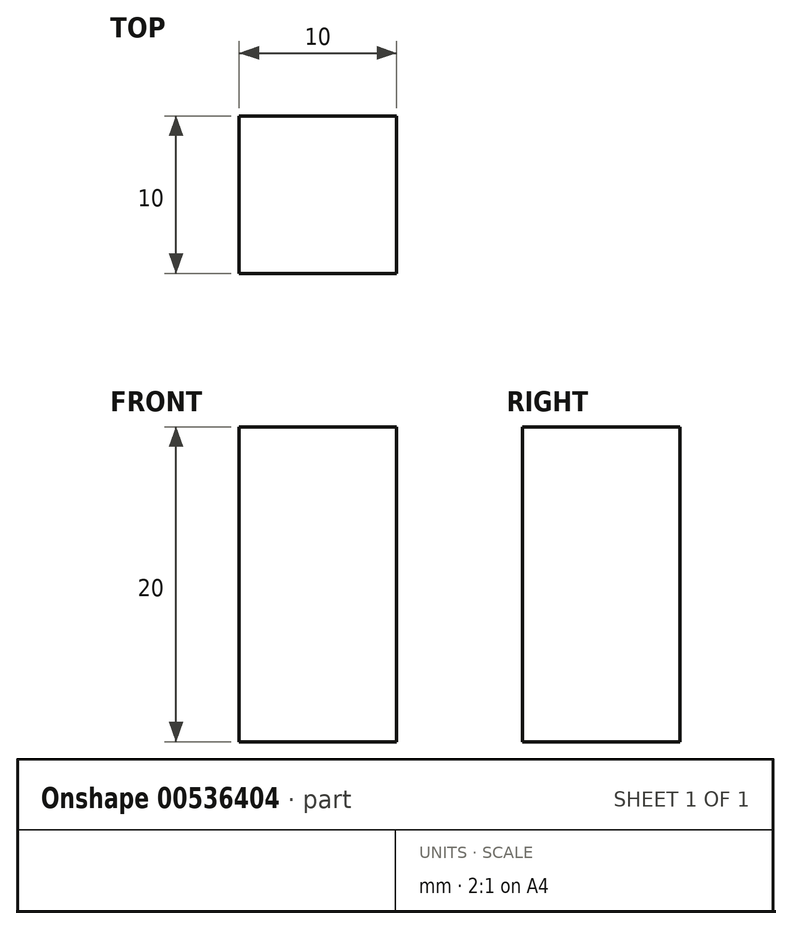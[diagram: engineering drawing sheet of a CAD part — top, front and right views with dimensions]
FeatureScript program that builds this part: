
annotation { "Feature Type Name" : "Feature", "Feature Type Description" : "" }
export const myFeature = defineFeature(function(context is Context, id is Id, definition is map)
    precondition{}
    {
        {
            var Q0;
            Q0=qCreatedBy(makeId("Front.planeOp"),FACE);
            var sketch = newSketch(context, id + "F0", { "sketchPlane" : qUnion([Q0])});
            skLineSegment(sketch, "E0.bottom", {"start": v(5, -10) * mm, "end": v(-5, -10) * mm});
            skLineSegment(sketch, "E0.top", {"start": v(5, 10) * mm, "end": v(-5, 10) * mm});
            skLineSegment(sketch, "E0.left", {"start": v(5, -10) * mm, "end": v(5, 10) * mm});
            skLineSegment(sketch, "E0.right", {"start": v(-5, -10) * mm, "end": v(-5, 10) * mm});
            skPoint(sketch, "E0.middle", {"position": v(0, 0) * mm});
            skSolve(sketch);
        }
        {
            var Q0;
            Q0=qSketchRegion(id+"F0",true);
            extrude(context, id + "F1", {"entities" : qUnion([Q0]), "depth" : 10 * mm});
        }
    });
